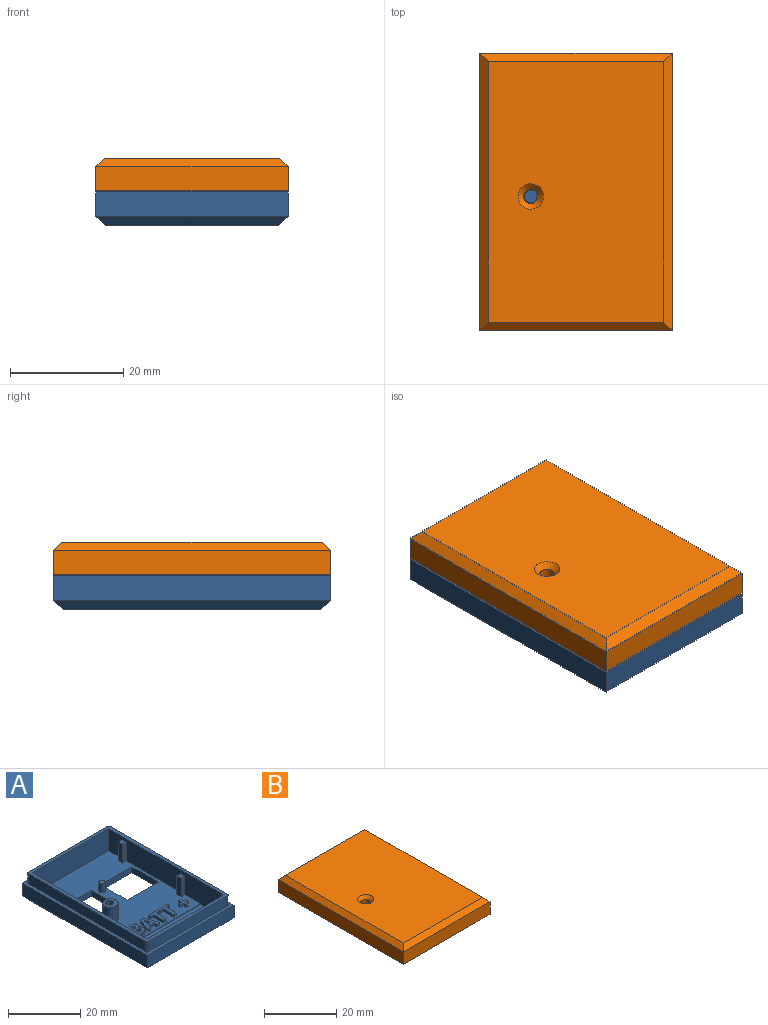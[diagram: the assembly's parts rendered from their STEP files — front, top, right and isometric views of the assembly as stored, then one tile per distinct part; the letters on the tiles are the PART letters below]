
ASSEMBLY  parts=2 mates=1
PART A: 136 faces, bbox 34x49x9.5 mm
  f0: plane 36x30mm, normal (0,0,1), area 754.5mm2, adj f1,f2,f6,f7,f8,f9,f10,f11
  f1: plane 44x7.7mm, normal (1,0,0), area 310.2mm2, adj f0,f2,f15,f20,f21,f22,f107,f109
  f2: plane 30x0.2mm, normal (0,-1,0), area 6mm2, adj f0,f1,f12,f20
  f3: plane 46x3.5mm, normal (-1,0,0), area 161mm2, adj f22,f127,f128,f131
  f4: plane 31x3.5mm, normal (0,-1,0), area 108.5mm2, adj f22,f127,f128,f129
  f5: plane 46x3.5mm, normal (1,0,0), area 161mm2, adj f22,f127,f129,f130
  f6: plane 12.2x2mm, normal (0,-1,0), area 24.4mm2, adj f0,f7,f16,f19
  f7: plane 10.3x2mm, normal (-1,0,0), area 20.6mm2, adj f0,f6,f8,f19
  f8: plane 12.2x2mm, normal (0,1,0), area 24.4mm2, adj f0,f7,f16,f19
  f9: plane 10.3x2mm, normal (1,0,0), area 20.6mm2, adj f0,f10,f17,f19
  f10: plane 12.2x2mm, normal (0,-1,0), area 24.4mm2, adj f0,f9,f11,f19
  f11: plane 10.3x2mm, normal (-1,0,0), area 20.6mm2, adj f0,f10,f17,f19
  f12: plane 44x7.7mm, normal (-1,0,0), area 310.2mm2, adj f0,f2,f13,f20,f21,f22,f115,f116
  f13: cylinder r=1mm len=7.7mm, axis (0,0,-1), area 12.1mm2, adj f12,f14,f20,f22
  f14: plane 28x7.7mm, normal (0,1,0), area 215.6mm2, adj f13,f15,f20,f22
  f15: cylinder r=1mm len=7.7mm, axis (0,0,-1), area 12.1mm2, adj f1,f14,f20,f22
  f16: plane 10.3x2mm, normal (1,0,0), area 20.6mm2, adj f0,f6,f8,f19
  f17: plane 12.2x2mm, normal (0,1,0), area 24.4mm2, adj f0,f9,f11,f19
  f18: plane 31x3.5mm, normal (0,1,0), area 108.5mm2, adj f22,f127,f130,f131
  f19: plane 45.5x30.5mm, normal (0,0,-1), area 1136.4mm2, adj f6,f7,f8,f9,f10,f11,f16,f17
  f20: plane 30x9mm, normal (0,0,1), area 269.6mm2, adj f1,f2,f12,f13,f14,f15
  f21: plane 30x7.5mm, normal (0,-1,0), area 225mm2, adj f0,f1,f12,f22
  f22: plane 47x32mm, normal (0,0,1), area 154.2mm2, adj f1,f3,f4,f5,f12,f13,f14,f15
  f23: cylinder r=1.1mm len=5.5mm, axis (0,0,-1), area 38.2mm2, adj f25,f26
  f24: cylinder r=2.12mm len=5.5mm, axis (0,0,-1), area 73.4mm2, adj f0,f25
  f25: plane 4.25x4.25mm, normal (0,0,1), area 10.4mm2, adj f23,f24
  f26: plane 2.21x2.21mm, normal (0,0,1), area 3.8mm2, adj f23
  f27: plane 0.9x0.82mm, normal (-1,0,0), area 0.7mm2, adj f0,f28,f30,f31
  f28: plane 1.77x0.9mm, normal (0,-1,0), area 1.6mm2, adj f0,f27,f29,f31
  f29: plane 0.9x0.82mm, normal (1,0,0), area 0.7mm2, adj f0,f28,f30,f31
  f30: plane 1.77x0.9mm, normal (0,1,0), area 1.6mm2, adj f0,f27,f29,f31
  f31: plane 1.77x0.82mm, normal (0,0,1), area 1.5mm2, adj f27,f28,f29,f30
  f32: plane 1.25x0.9mm, normal (1,0,0), area 1.1mm2, adj f33,f56,f57,f58
  f33: plane 0.9x0.63mm, normal (0,-1,0), area 0.6mm2, adj f32,f34,f57,f58
  f34: extruded ~0.9x0.86mm, area 1.1mm2, adj f33,f35,f57,f58
  f35: extruded ~0.9x0.49mm, area 0.5mm2, adj f34,f36,f57,f58
  f36: extruded ~0.9x0.62mm, area 0.6mm2, adj f35,f56,f57,f58
  f37: plane 0.9x0.59mm, normal (0,1,0), area 0.5mm2, adj f38,f54,f57,f59
  f38: plane 1.07x0.9mm, normal (1,0,0), area 1mm2, adj f37,f39,f57,f59
  f39: plane 0.9x0.54mm, normal (0,-1,0), area 0.5mm2, adj f38,f40,f57,f59
  f40: extruded ~0.9x0.64mm, area 0.6mm2, adj f39,f41,f57,f59
  f41: extruded ~0.9x0.4mm, area 0.4mm2, adj f40,f42,f57,f59
  f42: extruded ~0.9x0.42mm, area 0.4mm2, adj f41,f54,f57,f59
  f43: plane 1.5x0.9mm, normal (0,1,0), area 1.3mm2, adj f0,f44,f55,f57
  f44: plane 4.81x0.9mm, normal (-1,0,0), area 4.3mm2, adj f0,f43,f45,f57
  f45: plane 1.8x0.9mm, normal (0,-1,0), area 1.6mm2, adj f0,f44,f46,f57
  f46: extruded ~1.29x0.9mm, area 1.2mm2, adj f0,f45,f47,f57
  f47: extruded ~1.03x0.9mm, area 1.1mm2, adj f0,f46,f48,f57
  f48: extruded ~0.9x0.74mm, area 0.7mm2, adj f0,f47,f49,f57
  f49: extruded ~0.9x0.66mm, area 0.7mm2, adj f0,f48,f50,f57
  f50: plane 0.9x0.03mm, normal (1,0,0), area 0mm2, adj f0,f49,f51,f57
  f51: extruded ~0.9x0.54mm, area 0.6mm2, adj f0,f50,f52,f57
  f52: extruded ~0.9x0.71mm, area 0.7mm2, adj f0,f51,f53,f57
  f53: extruded ~0.93x0.9mm, area 1mm2, adj f0,f52,f55,f57
  f54: extruded ~0.9x0.6mm, area 0.6mm2, adj f37,f42,f57,f59
  f55: extruded ~1.49x0.9mm, area 1.4mm2, adj f0,f43,f53,f57
  f56: plane 0.9x0.66mm, normal (0,1,0), area 0.6mm2, adj f32,f36,f57,f58
  f57: plane 4.81x3.57mm, normal (0,0,1), area 12.6mm2, adj f32,f33,f34,f35,f36,f37,f38,f39
  f58: plane 1.49x1.25mm, normal (0,0,1), area 1.7mm2, adj f32,f33,f34,f35,f36,f56
  f59: plane 1.38x1.07mm, normal (0,0,1), area 1.3mm2, adj f37,f38,f39,f40,f41,f42,f54
  f60: extruded ~1.76x0.9mm, area 1.7mm2, adj f61,f71,f72,f73
  f61: plane 1.25x0.9mm, normal (0,1,0), area 1.1mm2, adj f60,f62,f72,f73
  f62: extruded ~2.08x0.9mm, area 2mm2, adj f61,f71,f72,f73
  f63: plane 1.15x0.9mm, normal (-0.96,-0.29,0), area 1.1mm2, adj f0,f64,f70,f72
  f64: plane 1.1x0.9mm, normal (0,-1,0), area 1mm2, adj f0,f63,f65,f72
  f65: plane 4.83x1.71mm, normal (0.94,0.33,0), area 4.6mm2, adj f0,f64,f66,f72
  f66: plane 1.25x0.9mm, normal (0,1,0), area 1.1mm2, adj f0,f65,f67,f72
  f67: plane 4.83x1.7mm, normal (-0.94,0.33,0), area 4.6mm2, adj f0,f66,f68,f72
  f68: plane 1.1x0.9mm, normal (0,-1,0), area 1mm2, adj f0,f67,f69,f72
  f69: plane 1.15x0.9mm, normal (0.96,-0.29,0), area 1.1mm2, adj f0,f68,f70,f72
  f70: plane 1.75x0.9mm, normal (0,-1,0), area 1.6mm2, adj f0,f63,f69,f72
  f71: extruded ~0.9x0.32mm, area 0.3mm2, adj f60,f62,f72,f73
  f72: plane 4.83x4.65mm, normal (0,0,1), area 10.6mm2, adj f60,f61,f62,f63,f64,f65,f66,f67
  f73: plane 2.08x1.25mm, normal (0,0,1), area 1.3mm2, adj f60,f61,f62,f71
  f74: plane 1.02x0.9mm, normal (0,-1,0), area 0.9mm2, adj f0,f75,f81,f82
  f75: plane 3.96x0.9mm, normal (1,0,0), area 3.6mm2, adj f0,f74,f76,f82
  f76: plane 1.31x0.9mm, normal (0,-1,0), area 1.2mm2, adj f0,f75,f77,f82
  f77: plane 0.9x0.85mm, normal (1,0,0), area 0.8mm2, adj f0,f76,f78,f82
  f78: plane 3.63x0.9mm, normal (0,1,0), area 3.3mm2, adj f0,f77,f79,f82
  f79: plane 0.9x0.85mm, normal (-1,0,0), area 0.8mm2, adj f0,f78,f80,f82
  f80: plane 1.31x0.9mm, normal (0,-1,0), area 1.2mm2, adj f0,f79,f81,f82
  f81: plane 3.96x0.9mm, normal (-1,0,0), area 3.6mm2, adj f0,f74,f80,f82
  f82: plane 4.81x3.63mm, normal (0,0,1), area 7.1mm2, adj f74,f75,f76,f77,f78,f79,f80,f81
  f83: plane 1.02x0.9mm, normal (0,-1,0), area 0.9mm2, adj f0,f84,f90,f91
  f84: plane 3.96x0.9mm, normal (1,0,0), area 3.6mm2, adj f0,f83,f85,f91
  f85: plane 1.31x0.9mm, normal (0,-1,0), area 1.2mm2, adj f0,f84,f86,f91
  f86: plane 0.9x0.85mm, normal (1,0,0), area 0.8mm2, adj f0,f85,f87,f91
  f87: plane 3.63x0.9mm, normal (0,1,0), area 3.3mm2, adj f0,f86,f88,f91
  f88: plane 0.9x0.85mm, normal (-1,0,0), area 0.8mm2, adj f0,f87,f89,f91
  f89: plane 1.31x0.9mm, normal (0,-1,0), area 1.2mm2, adj f0,f88,f90,f91
  f90: plane 3.96x0.9mm, normal (-1,0,0), area 3.6mm2, adj f0,f83,f89,f91
  f91: plane 4.81x3.63mm, normal (0,0,1), area 7.1mm2, adj f83,f84,f85,f86,f87,f88,f89,f90
  f92: plane 1.27x0.9mm, normal (0,-1,0), area 1.1mm2, adj f0,f93,f103,f104
  f93: plane 1.27x0.9mm, normal (-1,0,0), area 1.1mm2, adj f0,f92,f94,f104
  f94: plane 0.9x0.72mm, normal (0,-1,0), area 0.6mm2, adj f0,f93,f95,f104
  f95: plane 1.27x0.9mm, normal (1,0,0), area 1.1mm2, adj f0,f94,f96,f104
  f96: plane 1.27x0.9mm, normal (0,-1,0), area 1.1mm2, adj f0,f95,f97,f104
  f97: plane 0.9x0.72mm, normal (1,0,0), area 0.6mm2, adj f0,f96,f98,f104
  f98: plane 1.27x0.9mm, normal (0,1,0), area 1.1mm2, adj f0,f97,f99,f104
  f99: plane 1.28x0.9mm, normal (1,0,0), area 1.2mm2, adj f0,f98,f100,f104
  f100: plane 0.9x0.72mm, normal (0,1,0), area 0.6mm2, adj f0,f99,f101,f104
  f101: plane 1.28x0.9mm, normal (-1,0,0), area 1.2mm2, adj f0,f100,f102,f104
  f102: plane 1.27x0.9mm, normal (0,1,0), area 1.1mm2, adj f0,f101,f103,f104
  f103: plane 0.9x0.72mm, normal (-1,0,0), area 0.6mm2, adj f0,f92,f102,f104
  f104: plane 3.27x3.27mm, normal (0,0,1), area 4.2mm2, adj f92,f93,f94,f95,f96,f97,f98,f99
  f105: cylinder r=0.88mm len=3mm, axis (0,0,-1), area 16.5mm2, adj f0,f106
  f106: plane 1.75x1.75mm, normal (0,0,1), area 2.4mm2, adj f105
  f107: plane 6.3x1.5mm, normal (0,-1,0), area 9.4mm2, adj f0,f1,f108,f110
  f108: plane 6.3x1.7mm, normal (1,0,0), area 10.7mm2, adj f0,f107,f109,f110
  f109: plane 6.3x1.5mm, normal (0,1,0), area 9.4mm2, adj f0,f1,f108,f110
  f110: plane 1.7x1.5mm, normal (0,0,1), area 2.5mm2, adj f1,f107,f108,f109
  f111: plane 6.3x1.5mm, normal (0,-1,0), area 9.4mm2, adj f0,f1,f112,f114
  f112: plane 6.3x1.7mm, normal (1,0,0), area 10.7mm2, adj f0,f111,f113,f114
  f113: plane 6.3x1.5mm, normal (0,1,0), area 9.4mm2, adj f0,f1,f112,f114
  f114: plane 1.7x1.5mm, normal (0,0,1), area 2.5mm2, adj f1,f111,f112,f113
  f115: plane 6.3x1.5mm, normal (0,-1,0), area 9.5mm2, adj f0,f12,f117,f118
  f116: plane 6.3x1.5mm, normal (0,1,0), area 9.5mm2, adj f0,f12,f117,f118
  f117: plane 6.3x1.7mm, normal (-1,0,0), area 10.7mm2, adj f0,f115,f116,f118
  f118: plane 1.7x1.5mm, normal (0,0,1), area 2.6mm2, adj f12,f115,f116,f117
  f119: plane 6.3x1.5mm, normal (0,-1,0), area 9.5mm2, adj f0,f12,f121,f122
  f120: plane 6.3x1.5mm, normal (0,1,0), area 9.5mm2, adj f0,f12,f121,f122
  f121: plane 6.3x1.7mm, normal (-1,0,0), area 10.7mm2, adj f0,f119,f120,f122
  f122: plane 1.7x1.5mm, normal (0,0,1), area 2.6mm2, adj f12,f119,f120,f121
  f123: plane 49x4.25mm, normal (-1,0,0), area 208.3mm2, adj f124,f126,f127,f135
  f124: plane 34x4.25mm, normal (0,-1,0), area 144.5mm2, adj f123,f125,f127,f133
  f125: plane 49x4.25mm, normal (1,0,0), area 208.3mm2, adj f124,f126,f127,f132
  f126: plane 34x4.25mm, normal (0,1,0), area 144.5mm2, adj f123,f125,f127,f134
  f127: plane 49x34mm, normal (0,0,1), area 162.2mm2, adj f3,f4,f5,f18,f123,f124,f125,f126
  f128: cylinder r=0.5mm len=3.5mm, axis (0,0,1), area 2.7mm2, adj f3,f4,f22,f127
  f129: cylinder r=0.5mm len=3.5mm, axis (0,0,-1), area 2.7mm2, adj f4,f5,f22,f127
  f130: cylinder r=0.5mm len=3.5mm, axis (0,0,1), area 2.7mm2, adj f5,f18,f22,f127
  f131: cylinder r=0.5mm len=3.5mm, axis (0,0,-1), area 2.7mm2, adj f3,f18,f22,f127
  f132: plane 49x1.75mm, normal (0.71,0,-0.71), area 116.9mm2, adj f19,f125,f133,f134
  f133: plane 34x1.75mm, normal (0,-0.71,-0.71), area 79.8mm2, adj f19,f124,f132,f135
  f134: plane 34x1.75mm, normal (0,0.71,-0.71), area 79.8mm2, adj f19,f126,f132,f135
  f135: plane 49x1.75mm, normal (-0.71,0,-0.71), area 116.9mm2, adj f19,f123,f133,f134
PART B: 26 faces, bbox 34x49x5.8 mm
  f0: plane 32x3.25mm, normal (0,-1,0), area 104mm2, adj f7,f9,f11,f15
  f1: plane 35.75x27.5mm, normal (0,0,-1), area 963.5mm2, adj f12,f13,f14,f16,f24
  f2: plane 49x4.25mm, normal (1,0,0), area 208.3mm2, adj f3,f5,f7,f21
  f3: plane 34x4.25mm, normal (0,1,0), area 144.5mm2, adj f2,f4,f7,f20
  f4: plane 49x4.25mm, normal (-1,0,0), area 208.3mm2, adj f3,f5,f7,f22
  f5: plane 34x4.25mm, normal (0,-1,0), area 144.5mm2, adj f2,f4,f7,f23
  f6: plane 46x31mm, normal (0,0,1), area 1410.1mm2, adj f19,f20,f21,f22,f23
  f7: plane 49x34mm, normal (0,0,-1), area 162mm2, adj f0,f2,f3,f4,f5,f9,f10,f11
  f8: plane 32x7mm, normal (0,0,-1), area 224mm2, adj f9,f11,f24,f25
  f9: plane 47x4.25mm, normal (1,0,0), area 160.6mm2, adj f0,f7,f8,f10,f15,f24,f25
  f10: plane 32x2.75mm, normal (0,1,0), area 88mm2, adj f7,f9,f11,f25
  f11: plane 47x4.25mm, normal (-1,0,0), area 160.6mm2, adj f0,f7,f8,f10,f15,f24,f25
  f12: plane 35.75x0.5mm, normal (-1,0,0), area 17.8mm2, adj f1,f14,f15,f24
  f13: plane 35.75x0.5mm, normal (1,0,0), area 17.8mm2, adj f1,f14,f15,f24
  f14: plane 27.5x0.5mm, normal (0,-1,0), area 13.8mm2, adj f1,f12,f13,f15
  f15: plane 37.5x32mm, normal (0,0,-1), area 230.6mm2, adj f0,f9,f11,f12,f13,f14,f24
  f16: cylinder r=2.5mm len=5mm, axis (0,0,1), area 7.9mm2, adj f1,f17
  f17: plane 5x5mm, normal (0,0,-1), area 14.3mm2, adj f16,f18
  f18: cylinder r=1.3mm len=2.6mm, axis (0,0,1), area 12.7mm2, adj f17,f19
  f19: cone r=1.3mm half-angle=45deg, axis (0,0,1), area 15mm2, adj f6,f18
  f20: plane 34x1.5mm, normal (0,0.71,0.71), area 68.9mm2, adj f3,f6,f21,f22
  f21: plane 49x1.5mm, normal (0.71,0,0.71), area 100.8mm2, adj f2,f6,f20,f23
  f22: plane 49x1.5mm, normal (-0.71,0,0.71), area 100.8mm2, adj f4,f6,f20,f23
  f23: plane 34x1.5mm, normal (0,-0.71,0.71), area 68.9mm2, adj f5,f6,f21,f22
  f24: plane 32x1mm, normal (0,-0.71,-0.71), area 25.8mm2, adj f1,f8,f9,f11,f12,f13,f15
  f25: plane 32x1.5mm, normal (0,0.71,-0.71), area 67.9mm2, adj f8,f9,f10,f11
PLACE A t=(-15.24,-17.44,-80.25)mm
PLACE B t=(-15.24,-17.44,-118.25)mm
MATE fastened A.f22 <-> B.f15  axis (0,0,1) through (0.76,29.56,-70.75)mm
